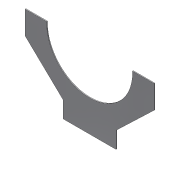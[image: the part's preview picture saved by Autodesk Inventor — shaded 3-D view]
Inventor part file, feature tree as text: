
AUTODESK INVENTOR PART (.ipt)
format: ipt  version: 2020.2 (Build 242310000, 310)  size: 92,160 bytes
history: native  units: mm
features: extrude x1, mirror x1, sketch x1
ambient origin geometry x8: Origin, YZ Plane, XZ Plane, XY Plane, X Axis, Y Axis, Z Axis, Center Point
bodies: Solid6 (feature_tree)
feature tree (3):
  extrude  "Extrusion7"  Depth=0.25mm
  mirror  "Mirror5"
  sketch  "Sketch11"  dims[d82=39.0mm d83=26.0mm d84=16.0mm d85=23.0mm d86=7.0mm d87=5.0mm d88=9.5mm d89=0.25mm d90=0.0mm]
